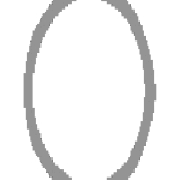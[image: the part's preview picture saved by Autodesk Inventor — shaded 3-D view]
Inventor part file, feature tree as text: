
AUTODESK INVENTOR PART (.ipt)
format: ipt  version: 2021 (Build 250183000, 183)  size: 154,112 bytes
history: native  units: in
note: dims shown in document units (in); Inventor stores cm internally (conversion verified against a paired STEP export)
features: other x5, sketch x2, sweep x1, plane x1
ambient origin geometry x8: Origin, YZ Plane, XZ Plane, XY Plane, X Axis, Y Axis, Z Axis, Center Point
bodies: Solid1 (feature_tree), Body (feature_tree)
feature tree (9):
  other  "Driven Length"
  other  "Frame Generator"
  other  "Start Plane"
  other  "End Plane"
  sweep  "Sweep Path"
  other  "Orientation Work Plane"
  sketch  "Sketch2"  dims[d0=1.0in d1=0.065in]
  plane  "Work Plane3"
  sketch  "Sketch3"  dims[d2=18.9842in d4=-0.0in d5=18.9842in d8=90.0deg d9=18.9842in d10=0.0in d11=0.0in]
